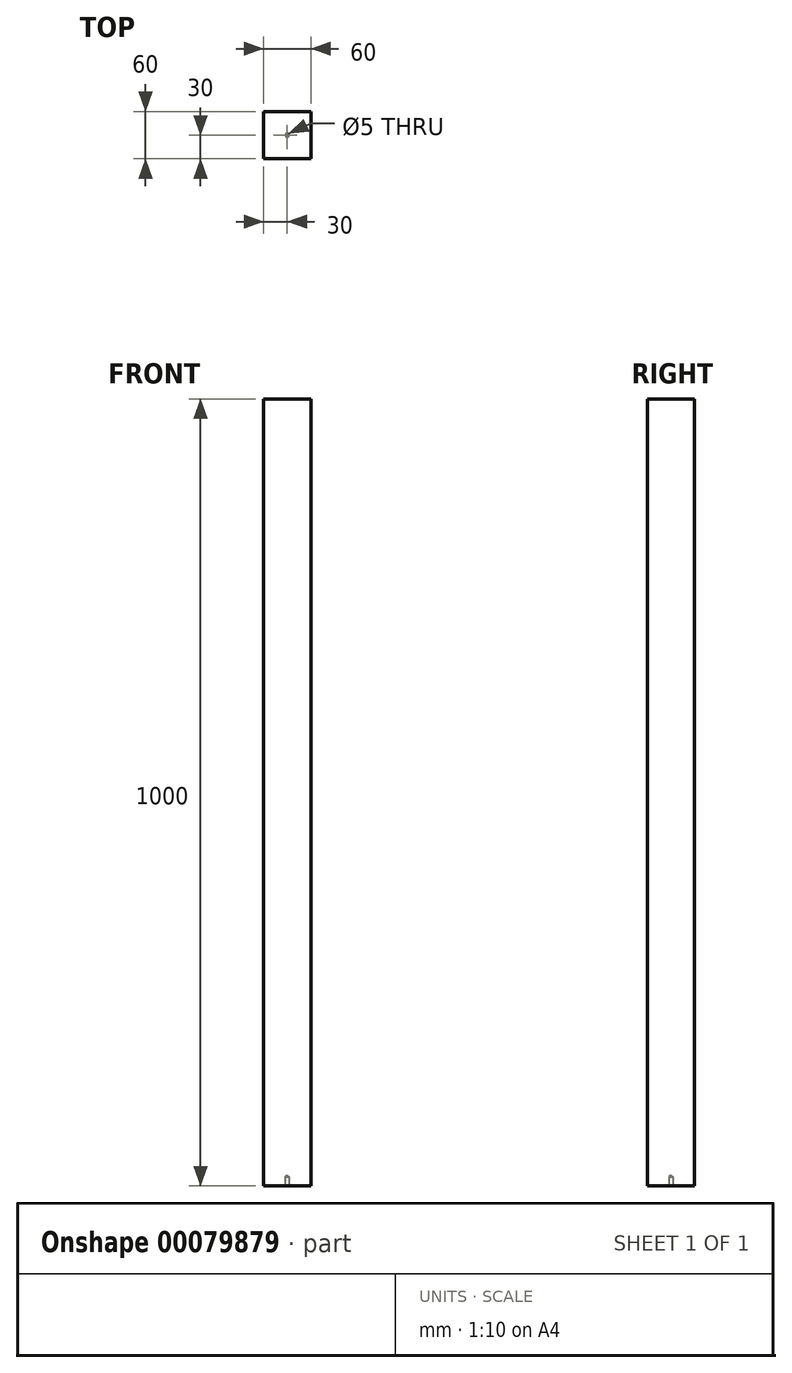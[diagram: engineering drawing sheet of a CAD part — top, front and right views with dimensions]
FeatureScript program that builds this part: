
annotation { "Feature Type Name" : "Feature", "Feature Type Description" : "" }
export const myFeature = defineFeature(function(context is Context, id is Id, definition is map)
    precondition{}
    {
        {
            assignVariable(context, id + "F0", {"name" : "bed_column_height", "anyValue" : 1000});
        }
        {
            assignVariable(context, id + "F1", {"name" : "hole_diameter", "anyValue" : 5});
        }
        {
            assignVariable(context, id + "F2", {"name" : "hole_length", "anyValue" : 12});
        }
        {
            var Q0;
            Q0=qCreatedBy(makeId("Top.planeOp"),FACE);
            var sketch = newSketch(context, id + "F3", { "sketchPlane" : qUnion([Q0])});
            skLineSegment(sketch, "E0.bottom", {"start": v(0, 0) * mm, "end": v(60, 0) * mm});
            skLineSegment(sketch, "E0.top", {"start": v(0, 60) * mm, "end": v(60, 60) * mm});
            skLineSegment(sketch, "E0.left", {"start": v(0, 0) * mm, "end": v(0, 60) * mm});
            skLineSegment(sketch, "E0.right", {"start": v(60, 0) * mm, "end": v(60, 60) * mm});
            skSolve(sketch);
        }
        {
            var Q0;
            Q0=makeQuery(id+"F3.imprint","IMPRINT",FACE,{"disambiguationData":[TD([[makeQuery(id+"F3.imprint","IMPRINT",EDGE,{"derivedFrom":sQuery(id+"F3.wireOp",EDGE,"E0.bottom")}),1.0]])]});
            extrude(context, id + "F4", {"entities" : qUnion([Q0]), "depth" : (getVariable(context, 'bed_column_height')) * mm});
        }
        {
            var Q0;
            Q0=makeQuery(id+"F4.opExtrude","CAP_FACE",FACE,{"disambiguationData":[OSD([sQuery(id+"F3.wireOp",EDGE,"E0.bottom"),sQuery(id+"F3.wireOp",EDGE,"E0.top"),sQuery(id+"F3.wireOp",EDGE,"E0.left"),sQuery(id+"F3.wireOp",EDGE,"E0.right")])],"isStart":true});
            var sketch = newSketch(context, id + "F5", { "sketchPlane" : qUnion([Q0])});
            skPoint(sketch, "E1", {"position": v(30, -30) * mm});
            skPoint(sketch, "E1.positionSnap0", {"position": v(60, -30) * mm});
            skPoint(sketch, "E1.positionSnap1", {"position": v(30, 0) * mm});
            skSolve(sketch);
        }
        {
            var Q0;
            Q0=sQuery(id+"F5.wireOp",VERTEX,"E1");
            var Q1;
            Q1=makeQuery(id+"F4.opExtrude","SWEPT_BODY",BODY,{"disambiguationData":[OSD([sQuery(id+"F3.wireOp",EDGE,"E0.bottom"),sQuery(id+"F3.wireOp",EDGE,"E0.top"),sQuery(id+"F3.wireOp",EDGE,"E0.left"),sQuery(id+"F3.wireOp",EDGE,"E0.right")])]});
            hole(context, id + "F6", {"style" : HoleStyle.SIMPLE, "endStyle" : HoleEndStyle.BLIND, "holeDiameter" : (getVariable(context, 'hole_diameter')) * mm, "holeDepth" : (getVariable(context, 'hole_length')) * mm, "startFromSketch" : true, "locations" : qUnion([Q0]), "scope" : qUnion([Q1])});
        }
    });
